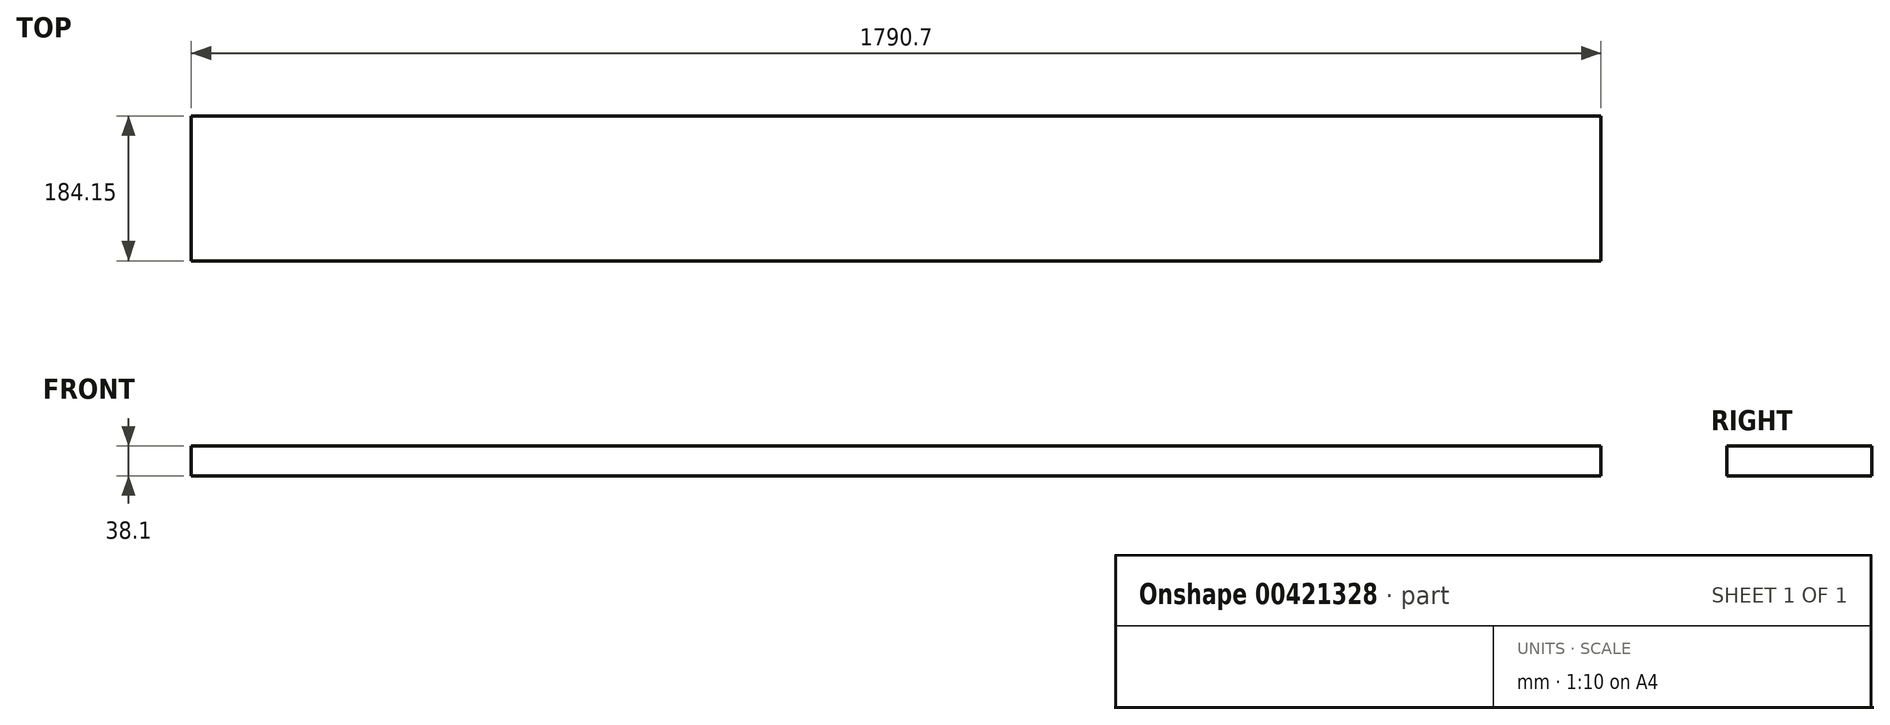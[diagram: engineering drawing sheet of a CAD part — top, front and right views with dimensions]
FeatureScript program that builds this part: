
annotation { "Feature Type Name" : "Feature", "Feature Type Description" : "" }
export const myFeature = defineFeature(function(context is Context, id is Id, definition is map)
    precondition{}
    {
        {
            var Q0;
            Q0=qCreatedBy(makeId("Top.planeOp"),FACE);
            var sketch = newSketch(context, id + "F0", { "sketchPlane" : qUnion([Q0])});
            skLineSegment(sketch, "E0.bottom", {"start": v(-49.01, -20.12) * mm, "end": v(1741.69, -20.12) * mm});
            skLineSegment(sketch, "E0.top", {"start": v(-49.01, 164.03) * mm, "end": v(1741.69, 164.03) * mm});
            skLineSegment(sketch, "E0.left", {"start": v(-49.01, -20.12) * mm, "end": v(-49.01, 164.03) * mm});
            skLineSegment(sketch, "E0.right", {"start": v(1741.69, -20.12) * mm, "end": v(1741.69, 164.03) * mm});
            skSolve(sketch);
        }
        {
            var Q0;
            Q0=makeQuery(id+"F0.imprint","IMPRINT",FACE,{"disambiguationData":[TD([[makeQuery(id+"F0.imprint","IMPRINT",EDGE,{"derivedFrom":sQuery(id+"F0.wireOp",EDGE,"E0.bottom")}),1.0]])]});
            extrude(context, id + "F1", {"entities" : qUnion([Q0]), "depth" : 38.1 * mm});
        }
    });
